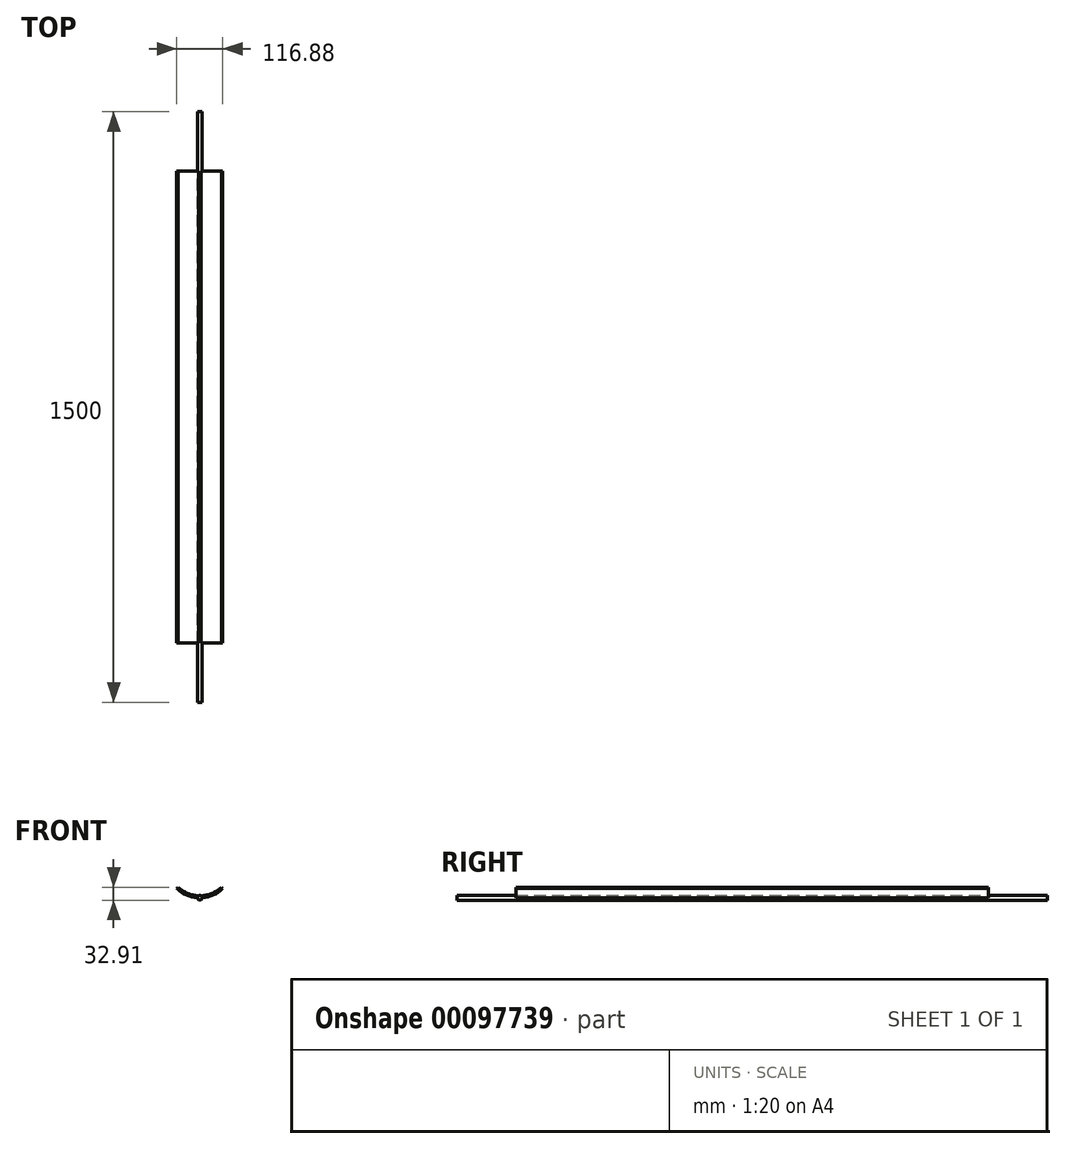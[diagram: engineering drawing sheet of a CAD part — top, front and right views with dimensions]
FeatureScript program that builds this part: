
annotation { "Feature Type Name" : "Feature", "Feature Type Description" : "" }
export const myFeature = defineFeature(function(context is Context, id is Id, definition is map)
    precondition{}
    {
        {
            var Q0;
            Q0=qCreatedBy(makeId("Front.planeOp"),FACE);
            var sketch = newSketch(context, id + "F0", { "sketchPlane" : qUnion([Q0])});
            skCircle(sketch, "E0", {"center": v(0, 0) * mm, "radius": 6 * mm});
            skSolve(sketch);
        }
        {
            var Q0;
            Q0=makeQuery(id+"F0.imprint","IMPRINT",FACE,{"disambiguationData":[TD([[makeQuery(id+"F0.imprint","IMPRINT",EDGE,{"derivedFrom":sQuery(id+"F0.wireOp",EDGE,"E0")}),1.0]])]});
            extrude(context, id + "F1", {"entities" : qUnion([Q0]), "endBound" : BoundingType.SYMMETRIC, "depth" : 1500 * mm});
        }
        {
            var Q0;
            Q0=qCreatedBy(makeId("Front.planeOp"),FACE);
            var sketch = newSketch(context, id + "F2", { "sketchPlane" : qUnion([Q0])});
            skArc(sketch, "E1", {"start": v(-58.44, 23.27) * mm, "mid": v(0, 0) * mm, "end": v(58.44, 23.27) * mm});
            skArc(sketch, "E2", {"start": v(-55, 26.9) * mm, "mid": v(0, 5) * mm, "end": v(55, 26.9) * mm});
            skLineSegment(sketch, "E3", {"start": v(-55, 26.9) * mm, "end": v(-58.44, 23.27) * mm});
            skLineSegment(sketch, "E4", {"start": v(55, 26.9) * mm, "end": v(58.44, 23.27) * mm});
            skLineSegment(sketch, "E5", {"start": v(0, 85) * mm, "end": v(0, 0) * mm, "construction": true});
            skLineSegment(sketch, "E6", {"start": v(-55, 26.9) * mm, "end": v(-56.45, 28.28) * mm, "construction": true});
            skLineSegment(sketch, "E7", {"start": v(55, 26.9) * mm, "end": v(56.45, 28.28) * mm, "construction": true});
            skSolve(sketch);
        }
        {
            var Q0;
            Q0=makeQuery(id+"F2.imprint","IMPRINT",FACE,{"disambiguationData":[TD([[makeQuery(id+"F2.imprint","IMPRINT",EDGE,{"derivedFrom":sQuery(id+"F2.wireOp",EDGE,"E1")}),1.0]])]});
            extrude(context, id + "F3", {"entities" : qUnion([Q0]), "operationType" : NewBodyOperationType.ADD, "endBound" : BoundingType.SYMMETRIC, "depth" : 1200 * mm});
        }
    });
